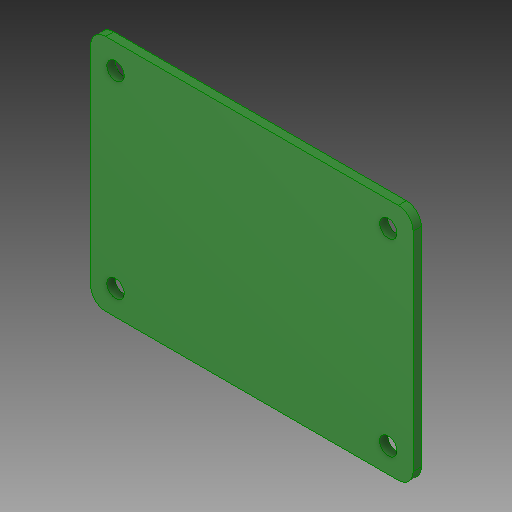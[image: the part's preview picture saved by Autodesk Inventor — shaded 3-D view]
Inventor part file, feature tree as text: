
AUTODESK INVENTOR PART (.ipt)
format: ipt  version: 2019.4 (Build 234330000, 330)  size: 123,904 bytes
history: native  units: mm
features: extrude x1, sketch x1, imported_body x1
ambient origin geometry x8: Origin, YZ Plane, XZ Plane, XY Plane, X Axis, Y Axis, Z Axis, Center Point
bodies: Solid1 (feature_tree)
feature tree (3):
  extrude  "Extrusion1"  Depth=3.0mm
  sketch  "Sketch1"  dims[d0=3.5mm d1=5.0mm d2=5.0mm d3=3.5mm d4=3.5mm d5=3.5mm d6=5.0mm d7=5.0mm d8=5.0mm d9=5.0mm d10=5.0mm d11=5.0mm d12=3.0mm d13=0.0mm]
  imported_body  "Base1"
